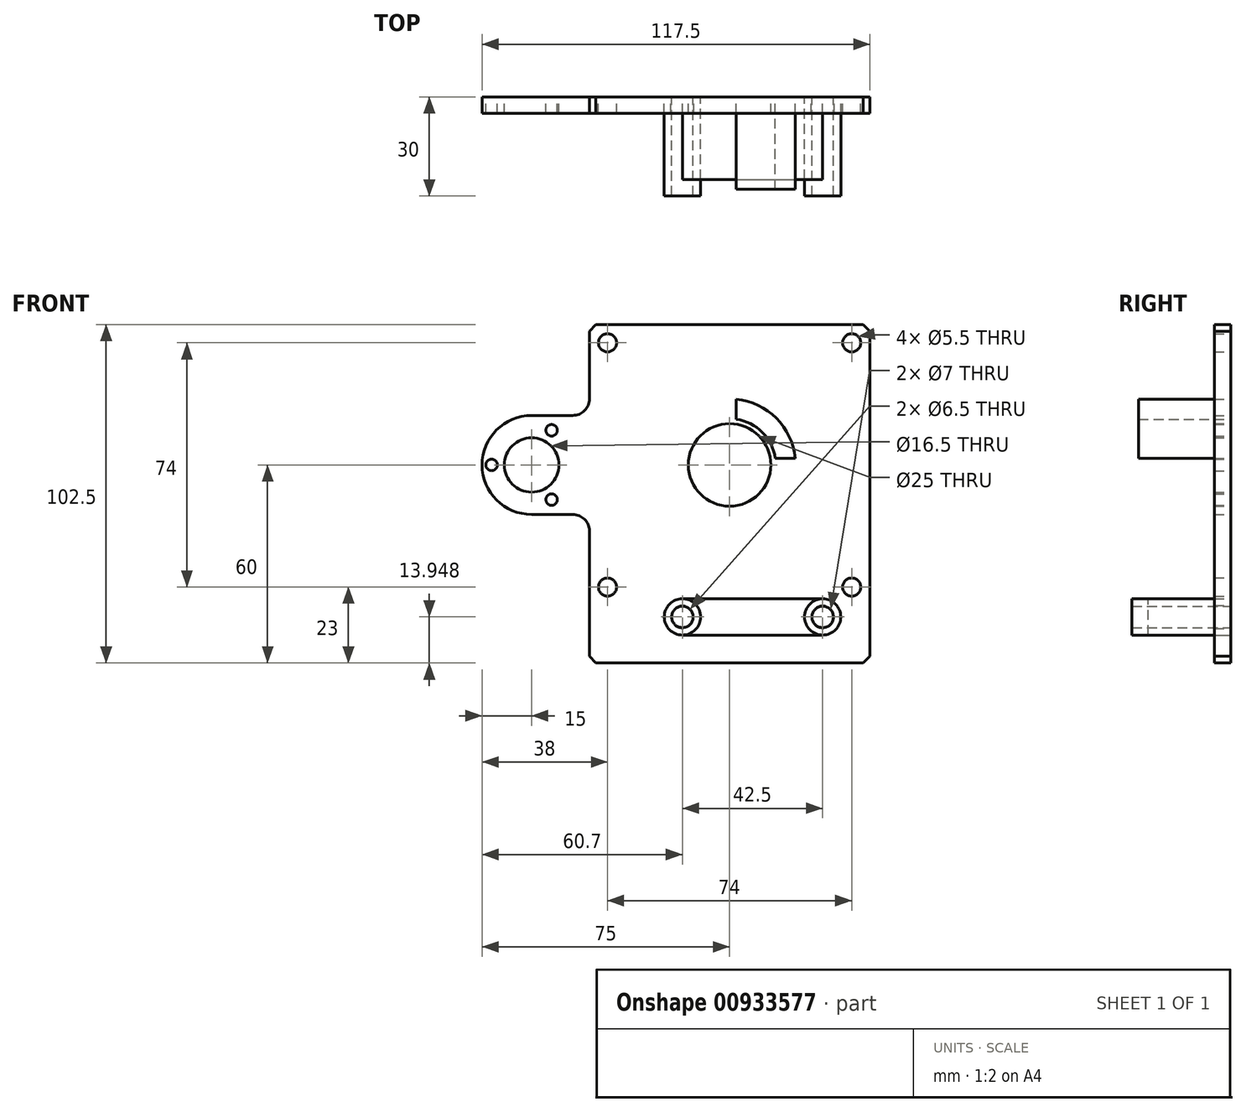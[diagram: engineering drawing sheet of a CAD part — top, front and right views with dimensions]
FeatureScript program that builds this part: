
annotation { "Feature Type Name" : "Feature", "Feature Type Description" : "" }
export const myFeature = defineFeature(function(context is Context, id is Id, definition is map)
    precondition{}
    {
        {
            var Q0;
            Q0=qCreatedBy(makeId("Front.planeOp"),FACE);
            var sketch = newSketch(context, id + "F0", { "sketchPlane" : qUnion([Q0])});
            skCircle(sketch, "E0", {"center": v(-14.3, -46.05) * mm, "radius": 3.25 * mm});
            skCircle(sketch, "E1", {"center": v(28.2, -46.05) * mm, "radius": 3.25 * mm});
            skCircle(sketch, "E2", {"center": v(28.2, -46.05) * mm, "radius": 5.5 * mm});
            skCircle(sketch, "E3", {"center": v(-14.3, -46.05) * mm, "radius": 5.5 * mm});
            skSolve(sketch);
        }
        {
            var Q0;
            Q0 = qSketchRegion(id + "F0", true);
            extrude(context, id + "F1", {"entities" : qUnion([Q0]), "depth" : 30 * mm, "offsetDistance" : 25 * mm});
        }
        {
            var Q0;
            Q0=qCreatedBy(makeId("Front.planeOp"),FACE);
            var sketch = newSketch(context, id + "F2", { "sketchPlane" : qUnion([Q0])});
            skCircle(sketch, "E4", {"center": v(-60, 0) * mm, "radius": 8.25 * mm});
            skArc(sketch, "E5", {"start": v(-60, 15) * mm, "mid": v(-75, 0) * mm, "end": v(-60, -15) * mm});
            skPoint(sketch, "E6.middle", {"position": v(0, 0) * mm});
            skCircle(sketch, "E7", {"center": v(0, 0) * mm, "radius": 12.5 * mm});
            skLineSegment(sketch, "E8.bottom", {"start": v(-42.5, 42.5) * mm, "end": v(42.5, 42.5) * mm});
            skLineSegment(sketch, "E8.top", {"start": v(-42.5, -60) * mm, "end": v(42.5, -60) * mm});
            skLineSegment(sketch, "E8.left", {"start": v(-42.5, 42.5) * mm, "end": v(-42.5, 20) * mm});
            skLineSegment(sketch, "E8.right", {"start": v(42.5, 42.5) * mm, "end": v(42.5, -60) * mm});
            skCircle(sketch, "E9", {"center": v(-14.3, -46.05) * mm, "radius": 3.5 * mm});
            skCircle(sketch, "E10", {"center": v(28.2, -46.05) * mm, "radius": 3.5 * mm});
            skLineSegment(sketch, "E11", {"start": v(-72.12, 0) * mm, "end": v(-53.94, 10.5) * mm, "construction": true});
            skLineSegment(sketch, "E12", {"start": v(-53.94, 10.5) * mm, "end": v(-53.94, -10.5) * mm, "construction": true});
            skLineSegment(sketch, "E13", {"start": v(-53.94, -10.5) * mm, "end": v(-72.12, 0) * mm, "construction": true});
            skLineSegment(sketch, "E14", {"start": v(-63.03, -5.25) * mm, "end": v(-58.46, 2.66) * mm, "construction": true});
            skCircle(sketch, "E15", {"center": v(-53.94, 10.5) * mm, "radius": 1.75 * mm});
            skCircle(sketch, "E16", {"center": v(-72.12, 0) * mm, "radius": 1.75 * mm});
            skCircle(sketch, "E17", {"center": v(-53.94, -10.5) * mm, "radius": 1.75 * mm});
            skLineSegment(sketch, "E18.bottom", {"start": v(-60, 15) * mm, "end": v(-47.5, 15) * mm});
            skLineSegment(sketch, "E18.top", {"start": v(-60, -15) * mm, "end": v(-47.5, -15) * mm});
            skArc(sketch, "E19", {"start": v(-42.5, -20) * mm, "mid": v(-43.96, -16.46) * mm, "end": v(-47.5, -15) * mm});
            skArc(sketch, "E20.MirrorCS", {"start": v(-42.5, 20) * mm, "mid": v(-43.96, 16.46) * mm, "end": v(-47.5, 15) * mm});
            skLineSegment(sketch, "E21.trimOffspring", {"start": v(-42.5, -20) * mm, "end": v(-42.5, -60) * mm});
            skPoint(sketch, "E22.trimOffspring.end.orphan", {"position": v(-42.5, -15) * mm});
            skCircle(sketch, "E23", {"center": v(-37, 37) * mm, "radius": 2.75 * mm});
            skCircle(sketch, "E24.MirrorC", {"center": v(37, 37) * mm, "radius": 2.75 * mm});
            skCircle(sketch, "E25.MirrorC", {"center": v(-37, -37) * mm, "radius": 2.75 * mm});
            skCircle(sketch, "E26.MirrorC", {"center": v(37, -37) * mm, "radius": 2.75 * mm});
            skSolve(sketch);
        }
        {
            var Q0;
            Q0 = qSketchRegion(id + "F2", true);
            extrude(context, id + "F3", {"entities" : qUnion([Q0]), "depth" : 5 * mm, "offsetDistance" : 25 * mm});
        }
        {
            var Q0;
            Q0=qCreatedBy(makeId("Front.planeOp"),FACE);
            var sketch = newSketch(context, id + "F4", { "sketchPlane" : qUnion([Q0])});
            skArc(sketch, "E27", {"start": v(2, 13.86) * mm, "mid": v(9.9, 9.9) * mm, "end": v(13.86, 2) * mm});
            skArc(sketch, "E28", {"start": v(2, 19.9) * mm, "mid": v(14.14, 14.14) * mm, "end": v(19.9, 2) * mm});
            skLineSegment(sketch, "E29", {"start": v(2, 19.9) * mm, "end": v(2, 13.86) * mm});
            skLineSegment(sketch, "E30", {"start": v(13.86, 2) * mm, "end": v(19.9, 2) * mm});
            skPoint(sketch, "E31.orphan", {"position": v(0, 20) * mm});
            skPoint(sketch, "E32.orphan", {"position": v(0, 14) * mm});
            skPoint(sketch, "E33.orphan", {"position": v(14, 0) * mm});
            skPoint(sketch, "E34.orphan", {"position": v(20, 0) * mm});
            skSolve(sketch);
        }
        {
            var Q0;
            Q0 = qSketchRegion(id + "F4", true);
            extrude(context, id + "F5", {"entities" : qUnion([Q0]), "depth" : 28 * mm, "offsetDistance" : 25 * mm});
        }
        {
            var Q0;
            Q0=qCreatedBy(makeId("Front.planeOp"),FACE);
            var sketch = newSketch(context, id + "F6", { "sketchPlane" : qUnion([Q0])});
            skLineSegment(sketch, "E35.bottom", {"start": v(-14.3, -40.55) * mm, "end": v(28.2, -40.55) * mm});
            skLineSegment(sketch, "E35.top", {"start": v(-14.3, -51.55) * mm, "end": v(28.2, -51.55) * mm});
            skPoint(sketch, "E35.middle", {"position": v(6.95, -46.05) * mm});
            skArc(sketch, "E36", {"start": v(-14.3, -51.55) * mm, "mid": v(-8.8, -46.05) * mm, "end": v(-14.3, -40.55) * mm});
            skArc(sketch, "E37", {"start": v(28.2, -40.55) * mm, "mid": v(22.7, -46.05) * mm, "end": v(28.2, -51.55) * mm});
            skSolve(sketch);
        }
        {
            var Q0;
            Q0 = qSketchRegion(id + "F6", true);
            extrude(context, id + "F7", {"entities" : qUnion([Q0]), "depth" : 25 * mm, "offsetDistance" : 25 * mm});
        }
        {
            var Q0;
            Q0=makeQuery(id+"F3.opExtrude","SWEPT_EDGE",EDGE,{"disambiguationData":[OSD([sQuery(id+"F2.wireOp",EDGE,"E8.bottom"),sQuery(id+"F2.wireOp",EDGE,"E8.left")])]});
            var Q1;
            Q1=makeQuery(id+"F3.opExtrude","SWEPT_EDGE",EDGE,{"disambiguationData":[OSD([sQuery(id+"F2.wireOp",EDGE,"E8.bottom"),sQuery(id+"F2.wireOp",EDGE,"E8.right")])]});
            var Q2;
            Q2=makeQuery(id+"F3.opExtrude","SWEPT_EDGE",EDGE,{"disambiguationData":[OSD([sQuery(id+"F2.wireOp",EDGE,"E8.top"),sQuery(id+"F2.wireOp",EDGE,"E8.right")])]});
            var Q3;
            Q3=makeQuery(id+"F3.opExtrude","SWEPT_EDGE",EDGE,{"disambiguationData":[OSD([sQuery(id+"F2.wireOp",EDGE,"E8.top"),sQuery(id+"F2.wireOp",EDGE,"E21.trimOffspring")])]});
            chamfer(context, id + "F8", {"entities" : qUnion([Q0, Q1, Q2, Q3]), "width" : 2 * mm, "tangentPropagation" : true});
        }
    });
